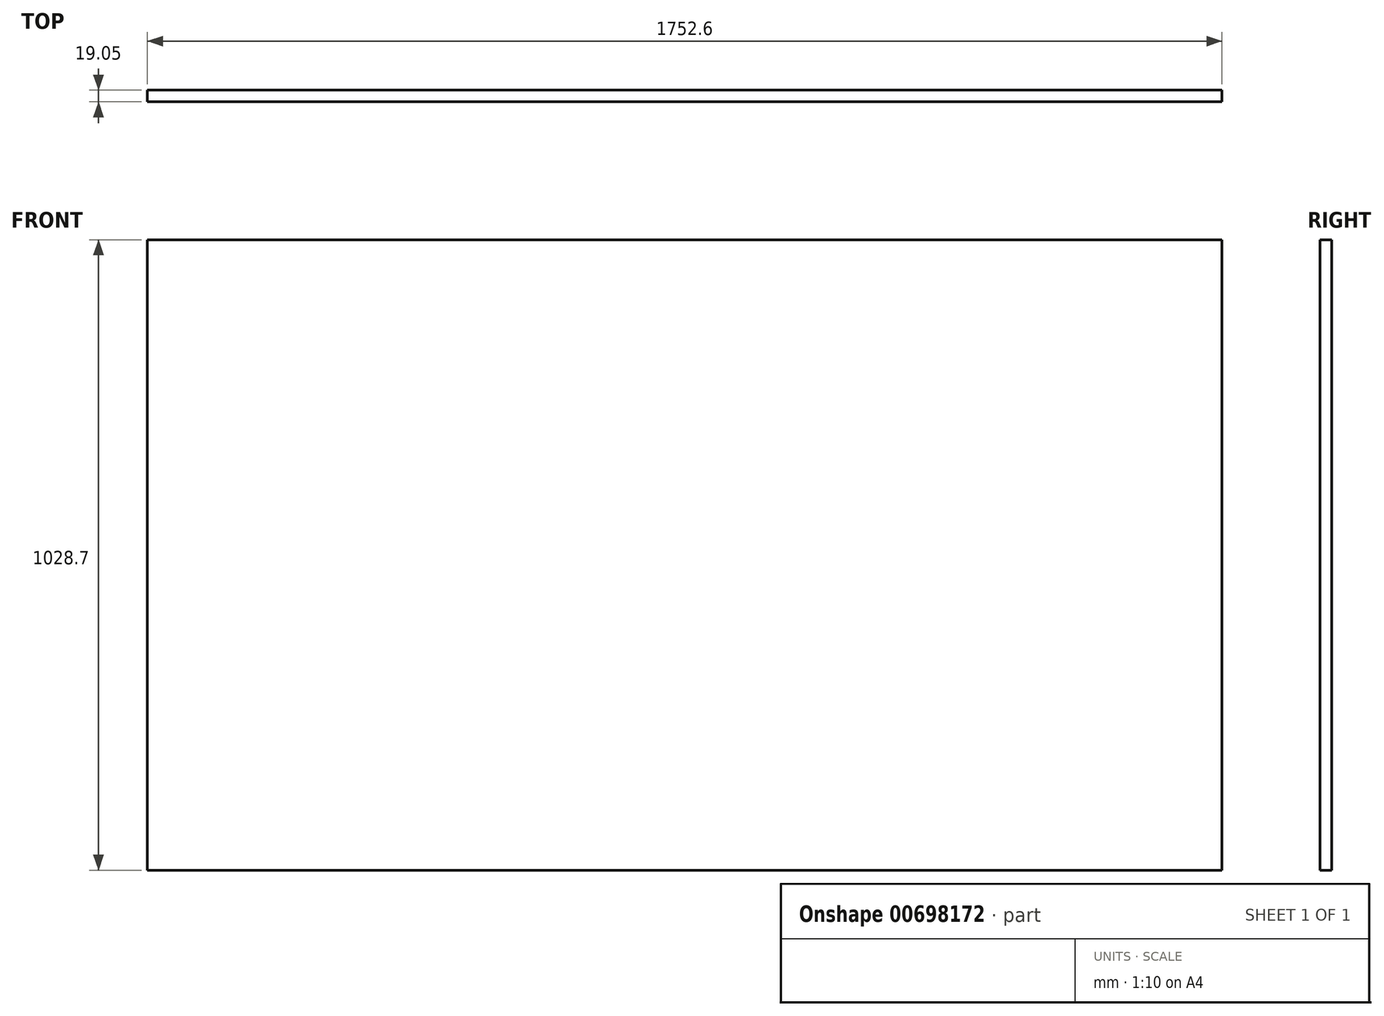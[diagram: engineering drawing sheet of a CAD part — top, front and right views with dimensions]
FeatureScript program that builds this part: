
annotation { "Feature Type Name" : "Feature", "Feature Type Description" : "" }
export const myFeature = defineFeature(function(context is Context, id is Id, definition is map)
    precondition{}
    {
        {
            var Q0;
            Q0=qCreatedBy(makeId("Front.planeOp"),FACE);
            var sketch = newSketch(context, id + "F0", { "sketchPlane" : qUnion([Q0])});
            skLineSegment(sketch, "E0.bottom", {"start": v(876.3, 514.35) * mm, "end": v(-876.3, 514.35) * mm});
            skLineSegment(sketch, "E0.top", {"start": v(876.3, -514.35) * mm, "end": v(-876.3, -514.35) * mm});
            skLineSegment(sketch, "E0.left", {"start": v(876.3, 514.35) * mm, "end": v(876.3, -514.35) * mm});
            skLineSegment(sketch, "E0.right", {"start": v(-876.3, 514.35) * mm, "end": v(-876.3, -514.35) * mm});
            skPoint(sketch, "E0.middle", {"position": v(0, 0) * mm});
            skSolve(sketch);
        }
        {
            var Q0;
            Q0=makeQuery(id+"F0.imprint","IMPRINT",FACE,{"disambiguationData":[TD([[makeQuery(id+"F0.imprint","IMPRINT",EDGE,{"derivedFrom":sQuery(id+"F0.wireOp",EDGE,"E0.bottom")}),1.0]])]});
            extrude(context, id + "F1", {"entities" : qUnion([Q0]), "depth" : 19.05 * mm, "offsetDistance" : 25.4 * mm});
        }
    });
